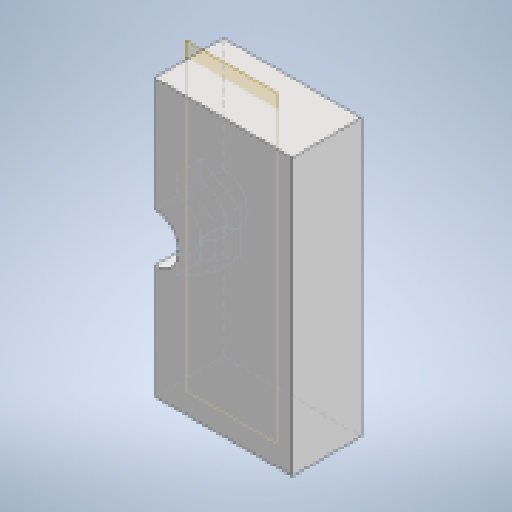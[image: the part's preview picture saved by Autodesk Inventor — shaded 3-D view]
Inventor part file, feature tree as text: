
AUTODESK INVENTOR PART (.ipt)
format: ipt  version: 2023 (Build 270158000, 158)  size: 184,320 bytes
history: native  units: mm
features: extrude x5, sketch x5, plane x1
ambient origin geometry x8: Origin, YZ Plane, XZ Plane, XY Plane, X Axis, Y Axis, Z Axis, Center Point
bodies: Solid1 (feature_tree)
feature tree (11):
  extrude  "Extrusion1"  Depth=20.0mm
  plane  "Work Plane1"
  extrude  "Extrusion2"  Depth=5.0mm
  extrude  "Extrusion3"  Depth=1.8mm
  extrude  "Extrusion4"  Depth=2.5mm
  extrude  "Extrusion5"  Depth=4.0mm
  sketch  "Sketch1"  dims[d0=20.0mm d1=20.0mm]
  sketch  "Sketch2"  dims[d10=5.0mm d11=0.0mm d12=5.5mm]
  sketch  "Sketch3"  dims[d13=1.8mm d14=0.0mm d15=3.5mm]
  sketch  "Sketch4"  dims[d16=8.0mm d17=0.0mm d18=2.5mm]
  sketch  "Sketch5"  dims[d19=2.5mm d20=2.5mm d21=2.5mm d22=2.6mm d23=2.6mm d24=25.0mm d25=0.0mm d26=4.0mm d27=4.0mm d28=4.0mm d29=0.0mm]
